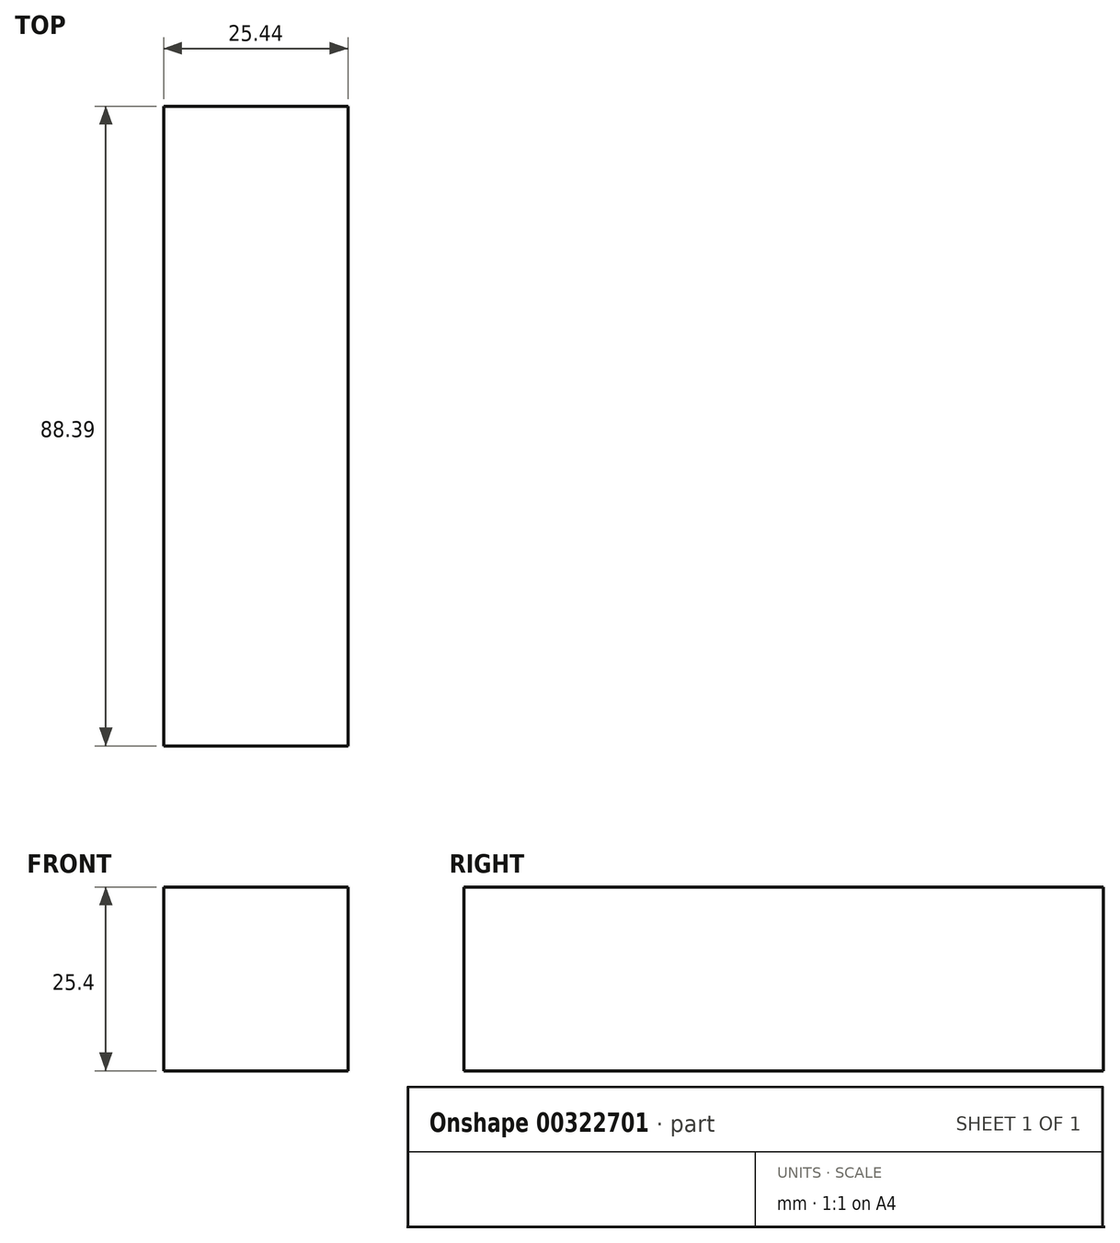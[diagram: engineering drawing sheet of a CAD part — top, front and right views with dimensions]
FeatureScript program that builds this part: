
annotation { "Feature Type Name" : "Feature", "Feature Type Description" : "" }
export const myFeature = defineFeature(function(context is Context, id is Id, definition is map)
    precondition{}
    {
        {
            var Q0;
            Q0=qCreatedBy(makeId("Top.planeOp"),FACE);
            var sketch = newSketch(context, id + "F0", { "sketchPlane" : qUnion([Q0])});
            skLineSegment(sketch, "E0.bottom", {"start": v(-54.98, 39.29) * mm, "end": v(-29.54, 39.29) * mm});
            skLineSegment(sketch, "E0.top", {"start": v(-54.98, -49.1) * mm, "end": v(-29.54, -49.1) * mm});
            skLineSegment(sketch, "E0.left", {"start": v(-54.98, 39.29) * mm, "end": v(-54.98, -49.1) * mm});
            skLineSegment(sketch, "E0.right", {"start": v(-29.54, 39.29) * mm, "end": v(-29.54, -49.1) * mm});
            skSolve(sketch);
        }
        {
            var Q0;
            Q0 = qSketchRegion(id + "F0", true);
            extrude(context, id + "F1", {"entities" : qUnion([Q0]), "depth" : 25.4 * mm});
        }
    });
